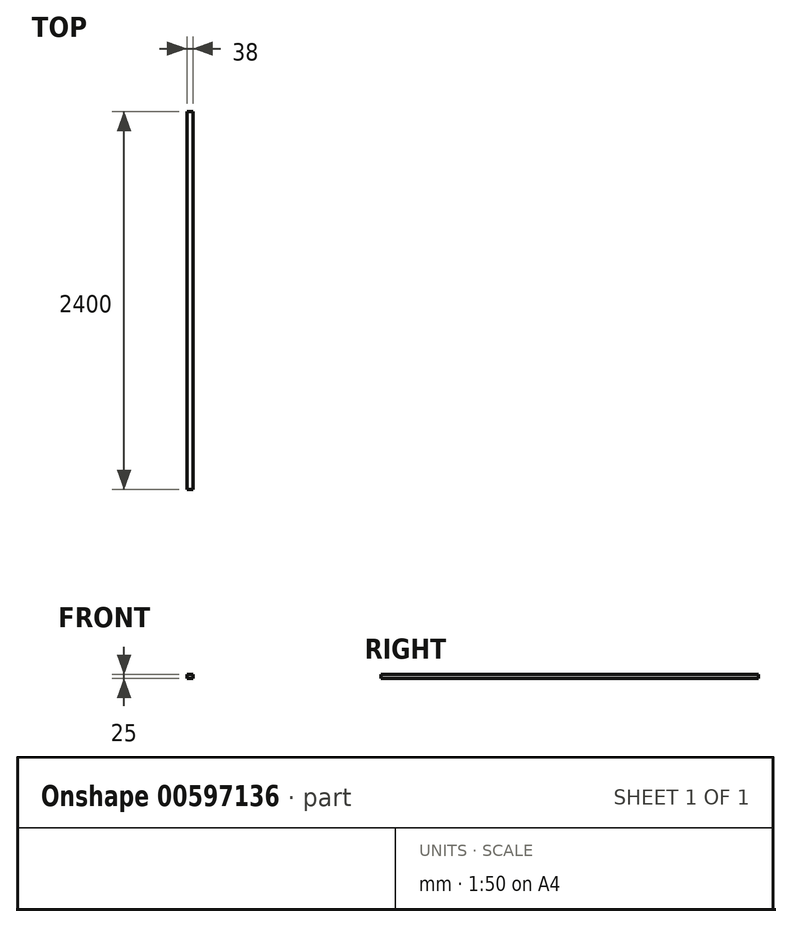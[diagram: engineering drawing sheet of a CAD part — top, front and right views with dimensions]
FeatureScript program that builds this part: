
annotation { "Feature Type Name" : "Feature", "Feature Type Description" : "" }
export const myFeature = defineFeature(function(context is Context, id is Id, definition is map)
    precondition{}
    {
        {
            var Q0;
            Q0=qCreatedBy(makeId("Front.planeOp"),FACE);
            var sketch = newSketch(context, id + "F0", { "sketchPlane" : qUnion([Q0])});
            skLineSegment(sketch, "E0.bottom", {"start": v(19, 12.5) * mm, "end": v(-19, 12.5) * mm});
            skLineSegment(sketch, "E0.top", {"start": v(19, -12.5) * mm, "end": v(-19, -12.5) * mm});
            skLineSegment(sketch, "E0.left", {"start": v(19, 12.5) * mm, "end": v(19, -12.5) * mm});
            skLineSegment(sketch, "E0.right", {"start": v(-19, 12.5) * mm, "end": v(-19, -12.5) * mm});
            skPoint(sketch, "E0.middle", {"position": v(0, 0) * mm});
            skSolve(sketch);
        }
        {
            var Q0;
            Q0 = qSketchRegion(id + "F0", true);
            extrude(context, id + "F1", {"entities" : qUnion([Q0]), "depth" : 2400 * mm, "offsetDistance" : 25 * mm});
        }
    });
